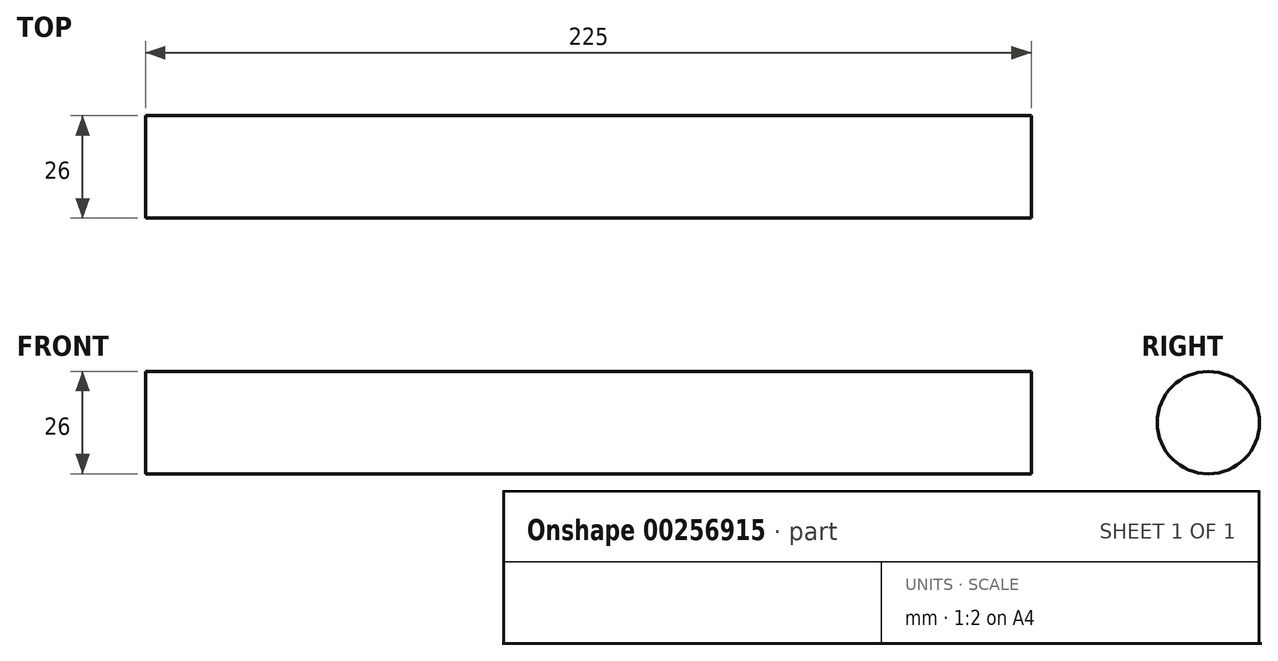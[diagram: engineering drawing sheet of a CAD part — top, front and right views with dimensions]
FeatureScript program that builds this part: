
annotation { "Feature Type Name" : "Feature", "Feature Type Description" : "" }
export const myFeature = defineFeature(function(context is Context, id is Id, definition is map)
    precondition{}
    {
        {
            var Q0;
            Q0=qCreatedBy(makeId("Right.planeOp"),FACE);
            var sketch = newSketch(context, id + "F0", { "sketchPlane" : qUnion([Q0])});
            skCircle(sketch, "E0", {"center": v(0, 0) * mm, "radius": 13 * mm});
            skSolve(sketch);
        }
        {
            var Q0;
            Q0=makeQuery(id+"F0.imprint","IMPRINT",FACE,{"disambiguationData":[TD([[makeQuery(id+"F0.imprint","IMPRINT",EDGE,{"derivedFrom":sQuery(id+"F0.wireOp",EDGE,"E0")}),1.0]])]});
            extrude(context, id + "F1", {"entities" : qUnion([Q0]), "oppositeDirection" : true, "depth" : 225 * mm});
        }
    });
